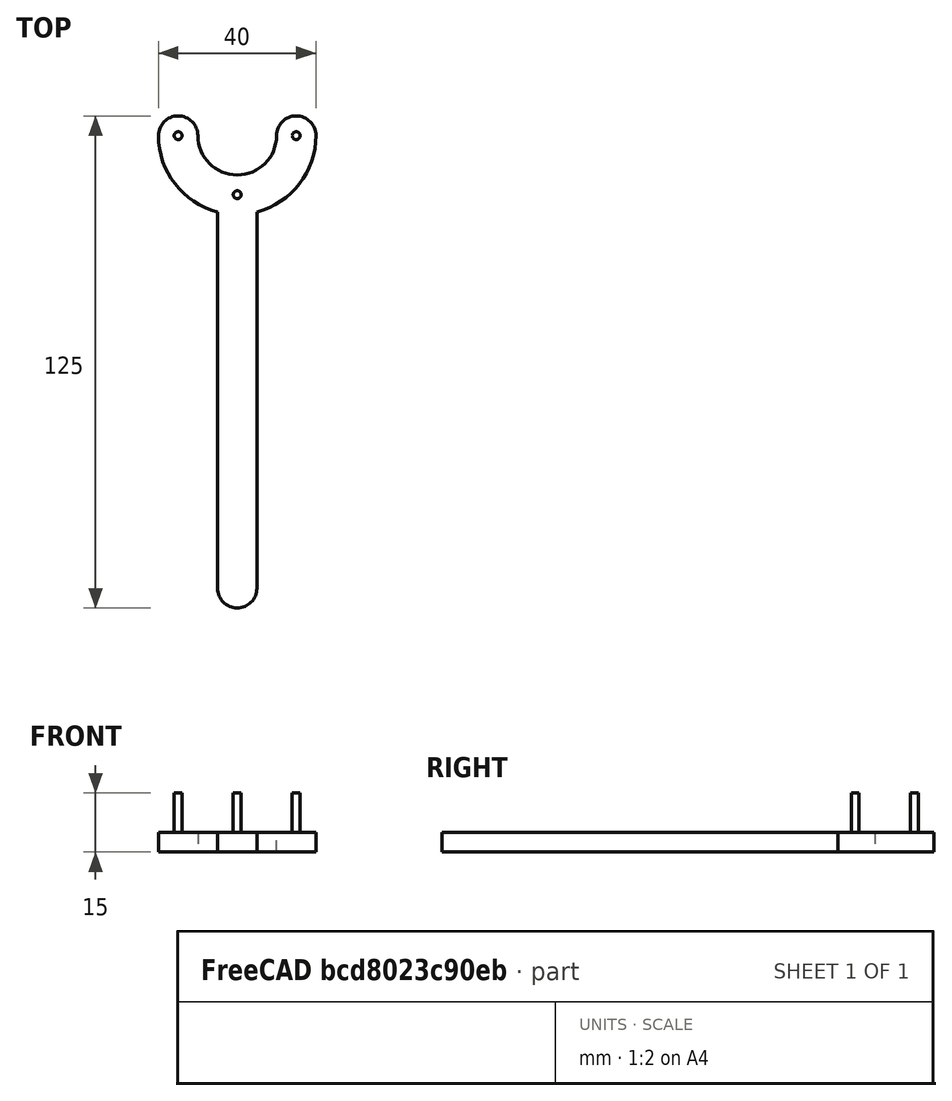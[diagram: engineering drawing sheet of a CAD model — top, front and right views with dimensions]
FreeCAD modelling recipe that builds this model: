
FCSTD DOCUMENT  (FreeCAD 0.20R)
Label: ConfigureablePinWrench
License: All rights reserved
LicenseURL: http://en.wikipedia.org/wiki/All_rights_reserved
objects: Part::Cylinder×8, Part::Cut×2, Part::Box×2, Part::MultiFuse×2, Spreadsheet::Sheet×1
note: 14 computed .brp shape members not serialized (recipe doc carries the construction recipe); baked Part::Feature solids carry a one-line shape summary decoded from their .brp

FEATURE [Spreadsheet::Sheet] Spreadsheet  label="WrenchParameters"
  cells = A2=Pin diameter; B2(diameter_pin)=1; A3=Pin ring diameter; B3(diameter_pinring)=30; A4=Material width; B4(width_material)=10; A5=Handle length; B5(length_handle)=100; A6=Handle width; B6(width_handle)=10; A7=Thickness; B7(thickness)=5; A8=Pin length; B8(length_pin)=10
FEATURE [Part::Cylinder] Cylinder
  Angle = 360
  AttacherType = Attacher::AttachEngine3D
  FirstAngle = 0
  Height = 5
  Radius = 10
  SecondAngle = 0
  expr: Height = <<WrenchParameters>>.thickness
  expr: Radius = <<WrenchParameters>>.diameter_pinring / 2 - <<WrenchParameters>>.width_material / 2
FEATURE [Part::Cylinder] Cylinder001
  Angle = 360
  AttacherType = Attacher::AttachEngine3D
  FirstAngle = 0
  Height = 5
  Radius = 20
  SecondAngle = 0
  expr: Height = <<WrenchParameters>>.thickness
  expr: Radius = <<WrenchParameters>>.diameter_pinring / 2 + <<WrenchParameters>>.width_material / 2
FEATURE [Part::Cut] Cut
  Base = -> Cylinder001
  Tool = -> Cylinder
FEATURE [Part::Box] Box  label="Cube"
  AttacherType = Attacher::AttachEngine3D
  Height = 5
  Length = 40
  Placement = pos=(-20,0,0) rot=(0,0,1;0rad)
  Width = 35
  expr: .Placement.Base.x = -(<<WrenchParameters>>.diameter_pinring + <<WrenchParameters>>.width_material) / 2
  expr: Height = <<WrenchParameters>>.thickness
  expr: Length = <<WrenchParameters>>.diameter_pinring + <<WrenchParameters>>.width_material
  expr: Width = <<WrenchParameters>>.diameter_pinring + <<WrenchParameters>>.width_material / 2
FEATURE [Part::Cut] Cut001
  Base = -> Cut
  Tool = -> Box
FEATURE [Part::Cylinder] Cylinder002
  Angle = 360
  AttacherType = Attacher::AttachEngine3D
  FirstAngle = 0
  Height = 5
  Placement = pos=(15,0,0) rot=(0,0,1;0rad)
  Radius = 5
  SecondAngle = 0
  expr: .Placement.Base.x = <<WrenchParameters>>.diameter_pinring / 2
  expr: Height = <<WrenchParameters>>.thickness
  expr: Radius = <<WrenchParameters>>.width_material / 2
FEATURE [Part::Cylinder] Cylinder003
  Angle = 360
  AttacherType = Attacher::AttachEngine3D
  FirstAngle = 0
  Height = 5
  Placement = pos=(-15,0,0) rot=(0,0,1;0rad)
  Radius = 5
  SecondAngle = 0
  expr: .Placement.Base.x = -<<WrenchParameters>>.diameter_pinring / 2
  expr: Height = <<WrenchParameters>>.thickness
  expr: Radius = <<WrenchParameters>>.width_material / 2
FEATURE [Part::MultiFuse] Fusion
  Shapes = -> [Cut001,Cylinder002,Cylinder003]
FEATURE [Part::Box] Box001  label="Cube001"
  AttacherType = Attacher::AttachEngine3D
  Height = 5
  Length = 10
  Placement = pos=(-5,-115,0) rot=(0,0,1;0rad)
  Width = 100
  expr: .Placement.Base.x = -<<WrenchParameters>>.width_handle / 2
  expr: .Placement.Base.y = -<<WrenchParameters>>.length_handle - <<WrenchParameters>>.diameter_pinring / 2
  expr: Height = <<WrenchParameters>>.thickness
  expr: Length = <<WrenchParameters>>.width_handle
  expr: Width = <<WrenchParameters>>.length_handle
FEATURE [Part::Cylinder] Cylinder004
  Angle = 360
  AttacherType = Attacher::AttachEngine3D
  FirstAngle = 0
  Height = 10
  Placement = pos=(0,-15,5) rot=(0,0,1;0rad)
  Radius = 1
  SecondAngle = 0
  expr: .Placement.Base.y = -<<WrenchParameters>>.diameter_pinring / 2
  expr: .Placement.Base.z = <<WrenchParameters>>.thickness
  expr: Height = <<WrenchParameters>>.length_pin
  expr: Radius = <<WrenchParameters>>.diameter_pin
FEATURE [Part::Cylinder] Cylinder005
  Angle = 360
  AttacherType = Attacher::AttachEngine3D
  FirstAngle = 0
  Height = 10
  Placement = pos=(15,0,5) rot=(0,0,1;0rad)
  Radius = 1
  SecondAngle = 0
  expr: .Placement.Base.x = <<WrenchParameters>>.diameter_pinring / 2
  expr: .Placement.Base.z = <<WrenchParameters>>.thickness
  expr: Height = <<WrenchParameters>>.length_pin
  expr: Radius = <<WrenchParameters>>.diameter_pin
FEATURE [Part::Cylinder] Cylinder006
  Angle = 360
  AttacherType = Attacher::AttachEngine3D
  FirstAngle = 0
  Height = 10
  Placement = pos=(-15,0,5) rot=(0,0,1;0rad)
  Radius = 1
  SecondAngle = 0
  expr: .Placement.Base.x = -<<WrenchParameters>>.diameter_pinring / 2
  expr: .Placement.Base.z = <<WrenchParameters>>.thickness
  expr: Height = <<WrenchParameters>>.length_pin
  expr: Radius = <<WrenchParameters>>.diameter_pin
FEATURE [Part::Cylinder] Cylinder007
  Angle = 360
  AttacherType = Attacher::AttachEngine3D
  FirstAngle = 0
  Height = 5
  Placement = pos=(0,-115,0) rot=(0,0,1;0rad)
  Radius = 5
  SecondAngle = 0
  expr: .Placement.Base.y = -<<WrenchParameters>>.length_handle - <<WrenchParameters>>.diameter_pinring / 2
  expr: Height = <<WrenchParameters>>.thickness
  expr: Radius = <<WrenchParameters>>.width_handle / 2
FEATURE [Part::MultiFuse] Fusion001  label="BaseConfigurablePinWrench"
  Shapes = -> [Fusion,Box001,Cylinder004,Cylinder005,Cylinder006,Cylinder007]
